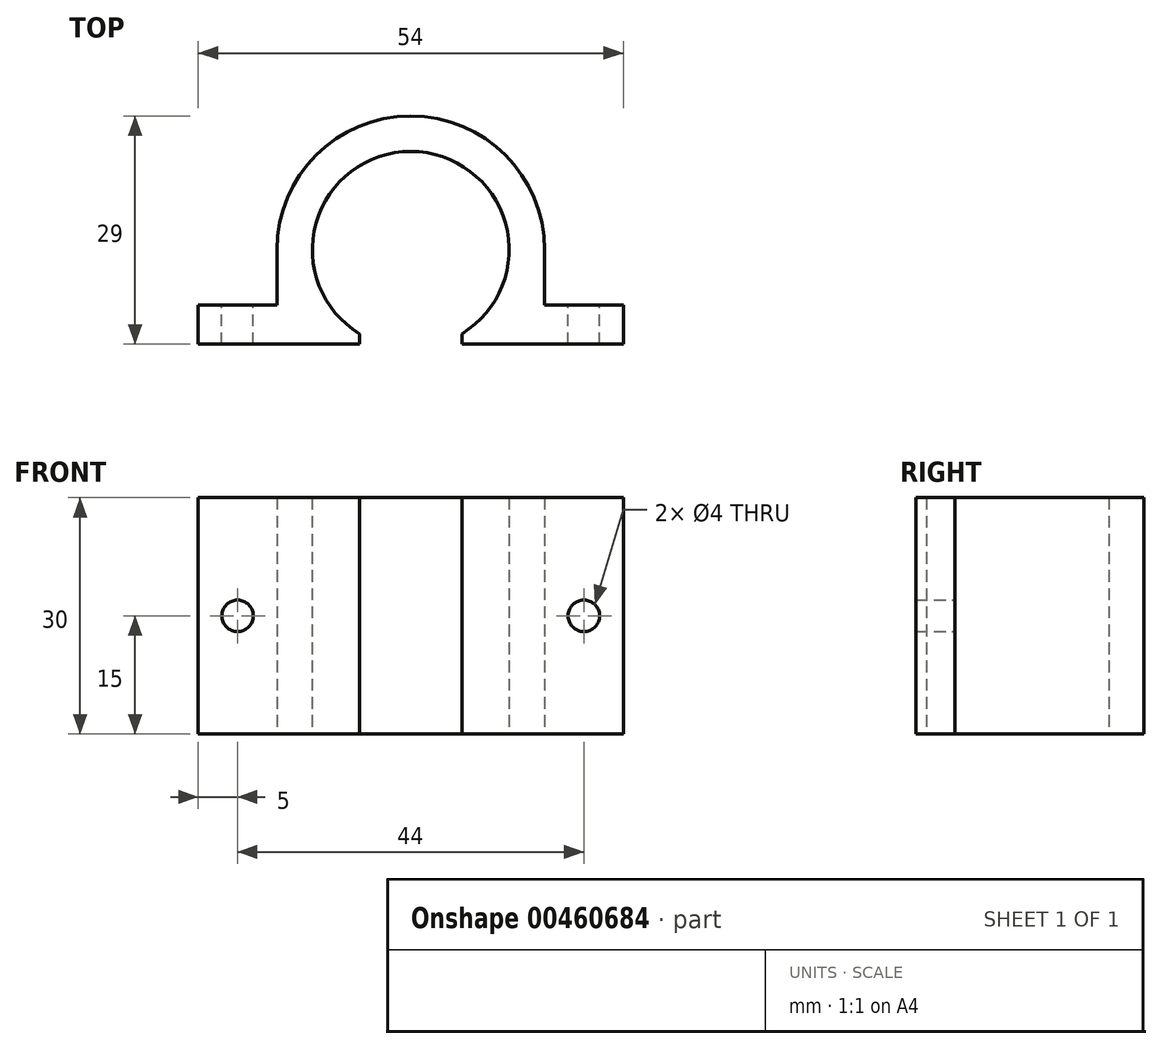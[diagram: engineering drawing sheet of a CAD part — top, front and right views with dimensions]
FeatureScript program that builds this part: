
annotation { "Feature Type Name" : "Feature", "Feature Type Description" : "" }
export const myFeature = defineFeature(function(context is Context, id is Id, definition is map)
    precondition{}
    {
        {
            var Q0;
            Q0=qCreatedBy(makeId("Top.planeOp"),FACE);
            var sketch = newSketch(context, id + "F0", { "sketchPlane" : qUnion([Q0])});
            skCircle(sketch, "E0", {"center": v(0, 0) * mm, "radius": 17 * mm});
            skCircle(sketch, "E1", {"center": v(0, 0) * mm, "radius": 12.5 * mm});
            skLineSegment(sketch, "E2.bottom", {"start": v(-17, 0) * mm, "end": v(17, 0) * mm});
            skLineSegment(sketch, "E2.top", {"start": v(-17, -17) * mm, "end": v(17, -17) * mm});
            skLineSegment(sketch, "E2.left", {"start": v(-17, 0) * mm, "end": v(-17, -17) * mm});
            skLineSegment(sketch, "E2.right", {"start": v(17, 0) * mm, "end": v(17, -17) * mm});
            skLineSegment(sketch, "E3", {"start": v(-23.43, 0) * mm, "end": v(35.21, 0) * mm, "construction": true});
            skLineSegment(sketch, "E4", {"start": v(0, 19.71) * mm, "end": v(0, -23.69) * mm, "construction": true});
            skLineSegment(sketch, "E5.bottom", {"start": v(-27, -12) * mm, "end": v(27, -12) * mm});
            skLineSegment(sketch, "E5.top", {"start": v(-27, -7) * mm, "end": v(27, -7) * mm});
            skLineSegment(sketch, "E5.left", {"start": v(-27, -12) * mm, "end": v(-27, -7) * mm});
            skLineSegment(sketch, "E5.right", {"start": v(27, -12) * mm, "end": v(27, -7) * mm});
            skLineSegment(sketch, "E6.bottom", {"start": v(-6.5, -12) * mm, "end": v(6.5, -12) * mm});
            skLineSegment(sketch, "E6.top", {"start": v(-6.5, -7) * mm, "end": v(6.5, -7) * mm});
            skLineSegment(sketch, "E6.left", {"start": v(-6.5, -12) * mm, "end": v(-6.5, -7) * mm});
            skLineSegment(sketch, "E6.right", {"start": v(6.5, -12) * mm, "end": v(6.5, -7) * mm});
            skSolve(sketch);
        }
        {
            var Q0;
            {var subQ5=sQuery(id+"F0.wireOp",EDGE,"E5.left");Q0=makeQuery(id+"F0.imprint","IMPRINT",FACE,{"disambiguationData":[TD([[makeQuery(id+"F0.imprint","IMPRINT",EDGE,{"derivedFrom":subQ5}),-1.0]])]});}
            var Q1;
            {var subQ5=sQuery(id+"F0.wireOp",EDGE,"E5.right");Q1=makeQuery(id+"F0.imprint","IMPRINT",FACE,{"disambiguationData":[TD([[makeQuery(id+"F0.imprint","IMPRINT",EDGE,{"derivedFrom":subQ5}),1.0]])]});}
            var Q2;
            {var subQ0=sQuery(id+"F0.wireOp",EDGE,"E2.left");var subQ3=sQuery(id+"F0.wireOp",EDGE,"E5.top");var subQ5=makeQuery(id+"F0.imprint","INTERSECT",VERTEX,{"derivedFrom":[subQ0,subQ3]});Q2=makeQuery(id+"F0.imprint","IMPRINT",FACE,{"disambiguationData":[TD([[makeQuery(id+"F0.imprint","IMPRINT",EDGE,{"disambiguationData":[TD([[subQ5,-1.0]])],"derivedFrom":subQ3}),1.0]])]});}
            var Q3;
            {var subQ0=sQuery(id+"F0.wireOp",EDGE,"E2.right");var subQ3=sQuery(id+"F0.wireOp",EDGE,"E5.top");var subQ5=makeQuery(id+"F0.imprint","INTERSECT",VERTEX,{"derivedFrom":[subQ0,subQ3]});Q3=makeQuery(id+"F0.imprint","IMPRINT",FACE,{"disambiguationData":[TD([[makeQuery(id+"F0.imprint","IMPRINT",EDGE,{"disambiguationData":[TD([[subQ5,1.0]])],"derivedFrom":subQ3}),1.0]])]});}
            var Q4;
            {var subQ0=sQuery(id+"F0.wireOp",EDGE,"E2.bottom");var subQ4=sQuery(id+"F0.wireOp",EDGE,"E1");var subQ5=makeQuery(id+"F0.imprint","INTERSECT",VERTEX,{"disambiguationData":[OD(0.0)],"derivedFrom":[subQ4,subQ0]});Q4=makeQuery(id+"F0.imprint","IMPRINT",FACE,{"disambiguationData":[TD([[makeQuery(id+"F0.imprint","IMPRINT",EDGE,{"disambiguationData":[TD([[subQ5,1.0]])],"derivedFrom":subQ4}),-1.0]])]});}
            var Q5;
            {var subQ0=sQuery(id+"F0.wireOp",EDGE,"E2.bottom");var subQ5=sQuery(id+"F0.wireOp",EDGE,"E1");var subQ6=makeQuery(id+"F0.imprint","INTERSECT",VERTEX,{"disambiguationData":[OD(0.0)],"derivedFrom":[subQ5,subQ0]});Q5=makeQuery(id+"F0.imprint","IMPRINT",FACE,{"disambiguationData":[TD([[makeQuery(id+"F0.imprint","IMPRINT",EDGE,{"disambiguationData":[TD([[subQ6,-1.0]])],"derivedFrom":subQ5}),-1.0]])]});}
            var Q6;
            {var subQ0=sQuery(id+"F0.wireOp",EDGE,"E5.top");var subQ1=sQuery(id+"F0.wireOp",EDGE,"E0");var subQ2=makeQuery(id+"F0.imprint","INTERSECT",VERTEX,{"disambiguationData":[OD(0.0)],"derivedFrom":[subQ1,subQ0]});Q6=makeQuery(id+"F0.imprint","IMPRINT",FACE,{"disambiguationData":[TD([[makeQuery(id+"F0.imprint","IMPRINT",EDGE,{"disambiguationData":[TD([[subQ2,-1.0]])],"derivedFrom":subQ1}),-1.0]])]});}
            var Q7;
            {var subQ0=sQuery(id+"F0.wireOp",EDGE,"E5.bottom");var subQ1=sQuery(id+"F0.wireOp",EDGE,"E0");var subQ2=makeQuery(id+"F0.imprint","INTERSECT",VERTEX,{"disambiguationData":[OD(1.0)],"derivedFrom":[subQ1,subQ0]});Q7=makeQuery(id+"F0.imprint","IMPRINT",FACE,{"disambiguationData":[TD([[makeQuery(id+"F0.imprint","IMPRINT",EDGE,{"disambiguationData":[TD([[subQ2,-1.0]])],"derivedFrom":subQ1}),-1.0]])]});}
            var Q8;
            {var subQ0=sQuery(id+"F0.wireOp",EDGE,"E2.bottom");var subQ5=sQuery(id+"F0.wireOp",EDGE,"E1");var subQ6=makeQuery(id+"F0.imprint","INTERSECT",VERTEX,{"disambiguationData":[OD(1.0)],"derivedFrom":[subQ5,subQ0]});Q8=makeQuery(id+"F0.imprint","IMPRINT",FACE,{"disambiguationData":[TD([[makeQuery(id+"F0.imprint","IMPRINT",EDGE,{"disambiguationData":[TD([[subQ6,1.0]])],"derivedFrom":subQ5}),-1.0]])]});}
            var Q9;
            {var subQ0=sQuery(id+"F0.wireOp",EDGE,"E5.top");var subQ1=sQuery(id+"F0.wireOp",EDGE,"E0");var subQ2=makeQuery(id+"F0.imprint","INTERSECT",VERTEX,{"disambiguationData":[OD(0.0)],"derivedFrom":[subQ1,subQ0]});Q9=makeQuery(id+"F0.imprint","IMPRINT",FACE,{"disambiguationData":[TD([[makeQuery(id+"F0.imprint","IMPRINT",EDGE,{"disambiguationData":[TD([[subQ2,-1.0]])],"derivedFrom":subQ1}),1.0]])]});}
            var Q10;
            {var subQ1=sQuery(id+"F0.wireOp",EDGE,"E0");var subQ5=sQuery(id+"F0.wireOp",EDGE,"E5.bottom");var subQ6=makeQuery(id+"F0.imprint","INTERSECT",VERTEX,{"disambiguationData":[OD(1.0)],"derivedFrom":[subQ1,subQ5]});Q10=makeQuery(id+"F0.imprint","IMPRINT",FACE,{"disambiguationData":[TD([[makeQuery(id+"F0.imprint","IMPRINT",EDGE,{"disambiguationData":[TD([[subQ6,-1.0]])],"derivedFrom":subQ1}),1.0]])]});}
            extrude(context, id + "F1", {"entities" : qUnion([Q0, Q1, Q2, Q3, Q4, Q5, Q6, Q7, Q8, Q9, Q10]), "depth" : 30 * mm, "offsetDistance" : 25 * mm});
        }
        {
            var Q0;
            Q0=qCreatedBy(makeId("Front.planeOp"),FACE);
            var sketch = newSketch(context, id + "F2", { "sketchPlane" : qUnion([Q0])});
            skCircle(sketch, "E7", {"center": v(-22, 15) * mm, "radius": 2 * mm});
            skCircle(sketch, "E8", {"center": v(22, 15) * mm, "radius": 2 * mm});
            skLineSegment(sketch, "E9", {"start": v(-32.99, 0) * mm, "end": v(35.36, 0) * mm, "construction": true});
            skSolve(sketch);
        }
        {
            var Q0;
            Q0 = qSketchRegion(id + "F2", true);
            var Q1;
            {var subQ0=sQuery(id+"F0.wireOp",EDGE,"E5.bottom");var subQ1=makeQuery(id+"F0.imprint","INTERSECT",VERTEX,{"derivedFrom":[sQuery(id+"F0.wireOp",EDGE,"E2.left"),subQ0]});Q1=makeQuery(id+"F1.opExtrude","SWEPT_FACE",FACE,{"disambiguationData":[OSD([subQ0]),TDD([makeQuery(id+"F0.imprint","IMPRINT",EDGE,{"disambiguationData":[TD([[subQ1,1.0]])],"derivedFrom":subQ0}),makeQuery(id+"F0.imprint","IMPRINT",EDGE,{"disambiguationData":[TD([[makeQuery(id+"F0.imprint","INTERSECT",VERTEX,{"derivedFrom":[subQ0,sQuery(id+"F0.wireOp",EDGE,"E6.left")]}),1.0]])],"derivedFrom":subQ0}),makeQuery(id+"F0.imprint","IMPRINT",EDGE,{"disambiguationData":[TD([[subQ1,-1.0]])],"derivedFrom":subQ0})])]});}
            var Q2;
            {var subQ0=sQuery(id+"F0.wireOp",EDGE,"E5.bottom");var subQ1=makeQuery(id+"F0.imprint","INTERSECT",VERTEX,{"derivedFrom":[sQuery(id+"F0.wireOp",EDGE,"E2.right"),subQ0]});Q2=makeQuery(id+"F1.opExtrude","SWEPT_FACE",FACE,{"disambiguationData":[OSD([subQ0]),TDD([makeQuery(id+"F0.imprint","IMPRINT",EDGE,{"disambiguationData":[TD([[subQ1,-1.0]])],"derivedFrom":subQ0}),makeQuery(id+"F0.imprint","IMPRINT",EDGE,{"disambiguationData":[TD([[makeQuery(id+"F0.imprint","INTERSECT",VERTEX,{"derivedFrom":[subQ0,sQuery(id+"F0.wireOp",EDGE,"E6.right")]}),-1.0]])],"derivedFrom":subQ0}),makeQuery(id+"F0.imprint","IMPRINT",EDGE,{"disambiguationData":[TD([[subQ1,1.0]])],"derivedFrom":subQ0})])]});}
            extrude(context, id + "F3", {"entities" : qUnion([Q0, Q1, Q2]), "operationType" : NewBodyOperationType.REMOVE, "depth" : 25 * mm, "offsetDistance" : 25 * mm});
        }
    });
